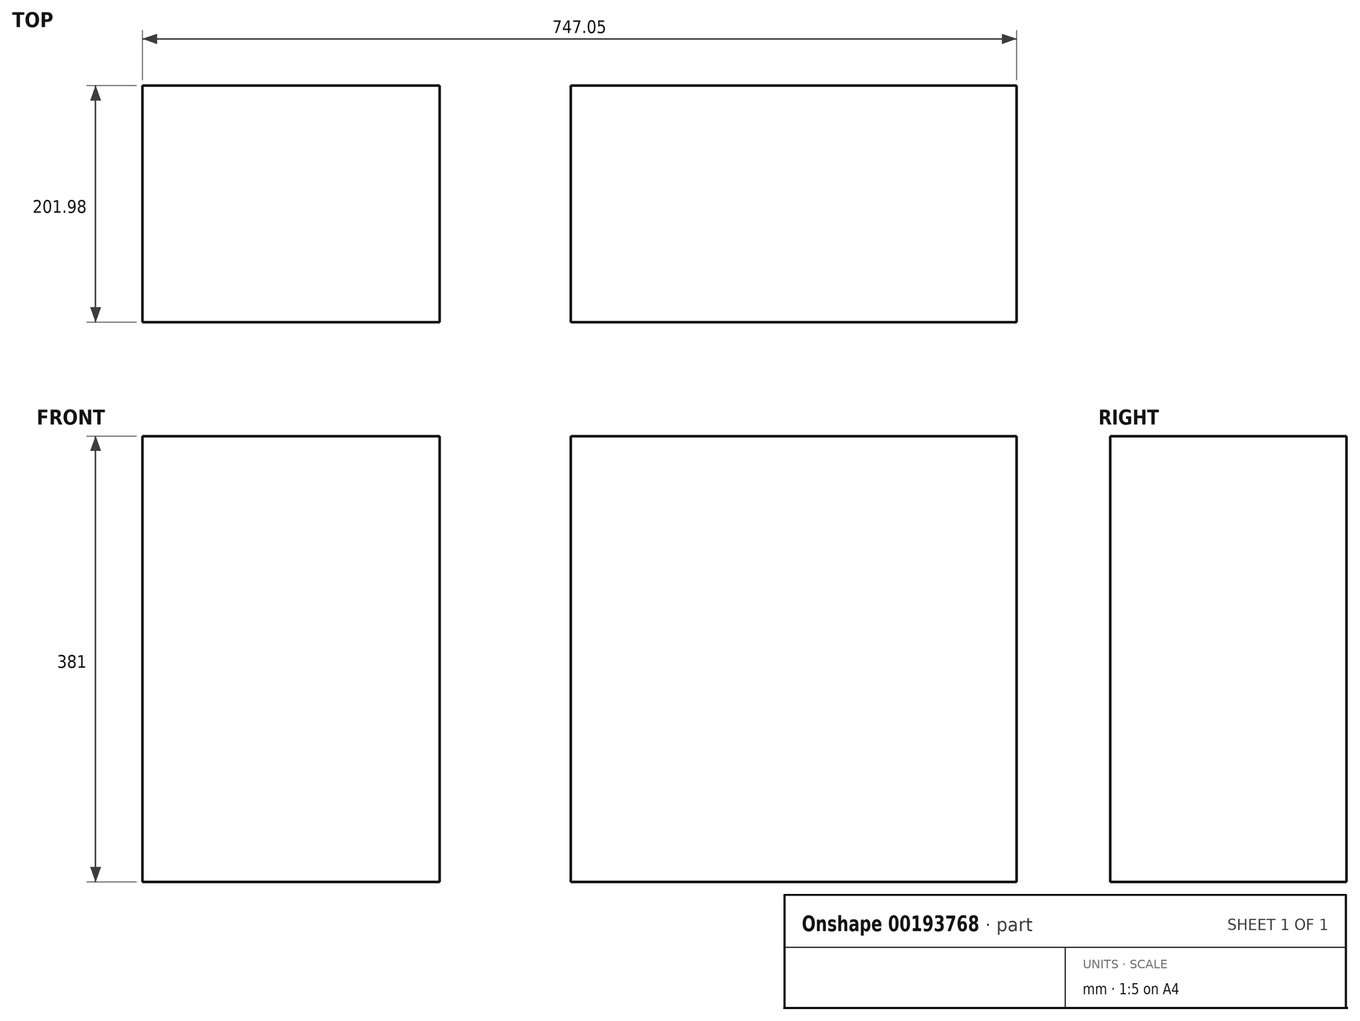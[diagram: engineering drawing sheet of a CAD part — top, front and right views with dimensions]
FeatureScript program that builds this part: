
annotation { "Feature Type Name" : "Feature", "Feature Type Description" : "" }
export const myFeature = defineFeature(function(context is Context, id is Id, definition is map)
    precondition{}
    {
        {
            var Q0;
            Q0=qCreatedBy(makeId("Top.planeOp"),FACE);
            var sketch = newSketch(context, id + "F0", { "sketchPlane" : qUnion([Q0])});
            skLineSegment(sketch, "E0.bottom", {"start": v(-180.93, 101) * mm, "end": v(200.07, 101) * mm});
            skLineSegment(sketch, "E0.top", {"start": v(-180.93, -101) * mm, "end": v(200.07, -101) * mm});
            skLineSegment(sketch, "E0.left", {"start": v(-180.93, 101) * mm, "end": v(-180.93, -101) * mm});
            skLineSegment(sketch, "E0.right", {"start": v(200.07, 101) * mm, "end": v(200.07, -101) * mm});
            skPoint(sketch, "E0.middle", {"position": v(9.57, 0) * mm});
            skLineSegment(sketch, "E1.bottom", {"start": v(-292.98, 101) * mm, "end": v(-546.98, 101) * mm});
            skLineSegment(sketch, "E1.top", {"start": v(-292.98, -101) * mm, "end": v(-546.98, -101) * mm});
            skLineSegment(sketch, "E1.left", {"start": v(-292.98, 101) * mm, "end": v(-292.98, -101) * mm});
            skLineSegment(sketch, "E1.right", {"start": v(-546.98, 101) * mm, "end": v(-546.98, -101) * mm});
            skSolve(sketch);
        }
        {
            var Q0;
            Q0=makeQuery(id+"F0.imprint","IMPRINT",FACE,{"disambiguationData":[TD([[makeQuery(id+"F0.imprint","IMPRINT",EDGE,{"derivedFrom":sQuery(id+"F0.wireOp",EDGE,"E1.bottom")}),1.0]])]});
            var Q1;
            Q1=makeQuery(id+"F0.imprint","IMPRINT",FACE,{"disambiguationData":[TD([[makeQuery(id+"F0.imprint","IMPRINT",EDGE,{"derivedFrom":sQuery(id+"F0.wireOp",EDGE,"E0.bottom")}),-1.0]])]});
            extrude(context, id + "F1", {"entities" : qUnion([Q0, Q1]), "depth" : 381 * mm});
        }
    });
